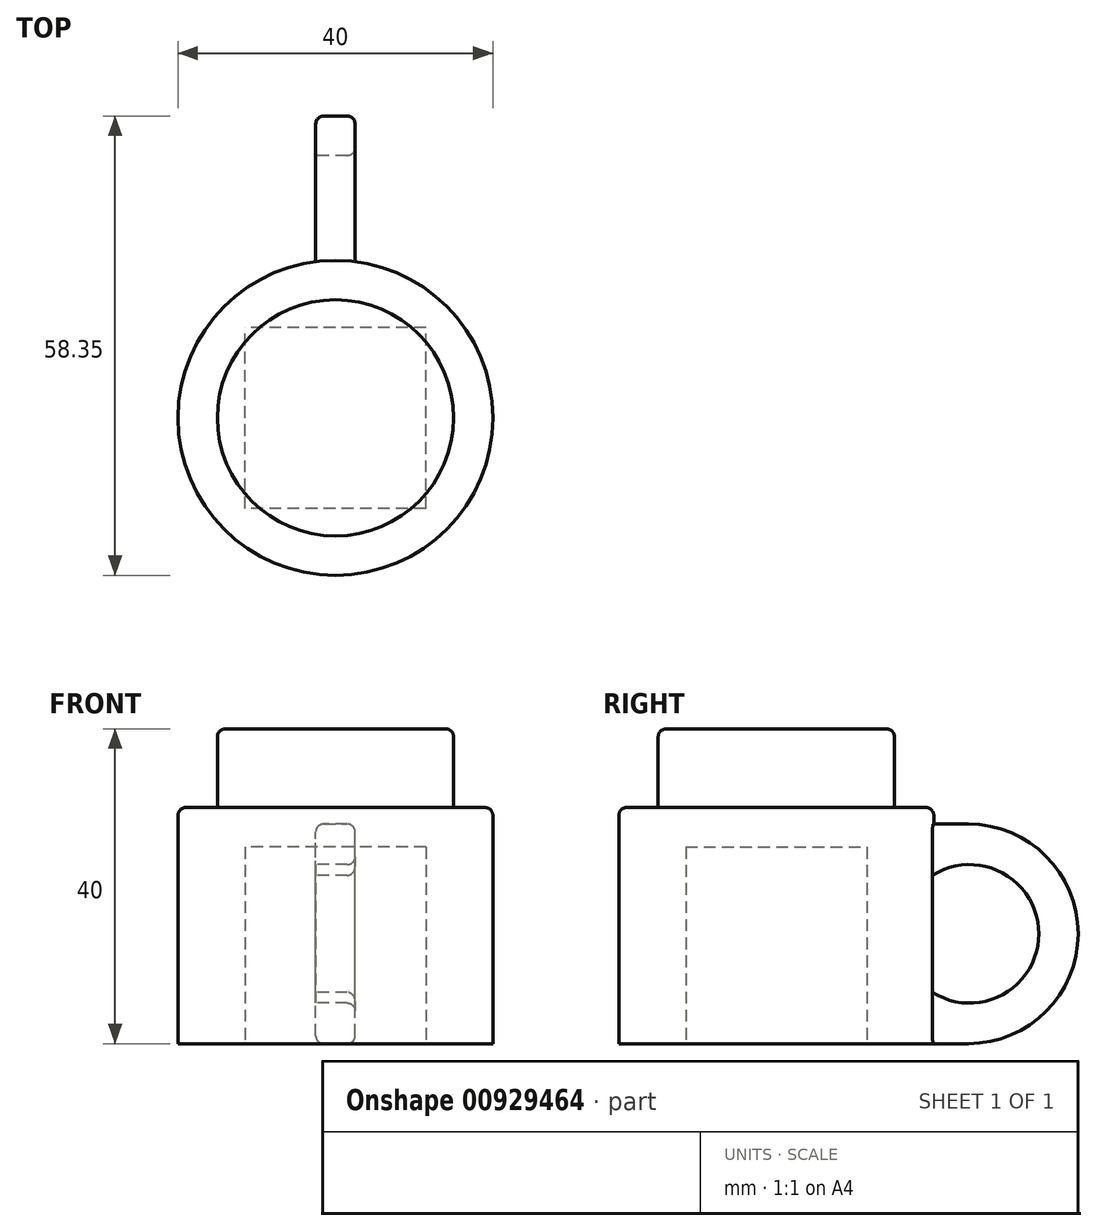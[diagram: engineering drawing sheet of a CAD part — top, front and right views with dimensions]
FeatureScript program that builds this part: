
annotation { "Feature Type Name" : "Feature", "Feature Type Description" : "" }
export const myFeature = defineFeature(function(context is Context, id is Id, definition is map)
    precondition{}
    {
        {
            var Q0;
            Q0=qCreatedBy(makeId("Top.planeOp"),FACE);
            var sketch = newSketch(context, id + "F0", { "sketchPlane" : qUnion([Q0])});
            skCircle(sketch, "E0", {"center": v(0, 0) * mm, "radius": 15 * mm});
            skSolve(sketch);
        }
        {
            var Q0;
            Q0=makeQuery(id+"F0.imprint","IMPRINT",FACE,{"disambiguationData":[TD([[makeQuery(id+"F0.imprint","IMPRINT",EDGE,{"derivedFrom":sQuery(id+"F0.wireOp",EDGE,"E0")}),1.0]])]});
            extrude(context, id + "F1", {"entities" : qUnion([Q0]), "depth" : 10 * mm, "offsetDistance" : 25 * mm});
        }
        {
            var Q0;
            Q0=qCreatedBy(makeId("Top.planeOp"),FACE);
            var sketch = newSketch(context, id + "F2", { "sketchPlane" : qUnion([Q0])});
            skCircle(sketch, "E1", {"center": v(0, 0) * mm, "radius": 20 * mm});
            skSolve(sketch);
        }
        {
            var Q0;
            Q0=makeQuery(id+"F2.imprint","IMPRINT",FACE,{"disambiguationData":[TD([[makeQuery(id+"F2.imprint","IMPRINT",EDGE,{"derivedFrom":sQuery(id+"F2.wireOp",EDGE,"E1")}),1.0]])]});
            extrude(context, id + "F3", {"entities" : qUnion([Q0]), "operationType" : NewBodyOperationType.ADD, "oppositeDirection" : true, "depth" : 30 * mm, "offsetDistance" : 25 * mm});
        }
        {
            var Q0;
            Q0=qCreatedBy(makeId("Right.planeOp"),FACE);
            var sketch = newSketch(context, id + "F4", { "sketchPlane" : qUnion([Q0])});
            skCircle(sketch, "E2", {"center": v(24.4, -16.05) * mm, "radius": 13.95 * mm});
            skPoint(sketch, "E2.first.point", {"position": v(11.59, -10.52) * mm});
            skPoint(sketch, "E2.second.point", {"position": v(37.23, -21.51) * mm});
            skPoint(sketch, "E2.third.point", {"position": v(35.11, -24.98) * mm});
            skLineSegment(sketch, "E3", {"start": v(-19.92, -30) * mm, "end": v(40.27, -30) * mm, "construction": true});
            skLineSegment(sketch, "E4", {"start": v(16.35, -30) * mm, "end": v(24.4, -30) * mm});
            skLineSegment(sketch, "E5", {"start": v(24.4, -30) * mm, "end": v(18.32, -26.87) * mm});
            skLineSegment(sketch, "E6", {"start": v(18.32, -26.87) * mm, "end": v(16.35, -30) * mm});
            skLineSegment(sketch, "E7", {"start": v(24.4, -2.1) * mm, "end": v(13.14, -2.1) * mm});
            skLineSegment(sketch, "E8", {"start": v(13.14, -2.1) * mm, "end": v(17.01, -7.58) * mm});
            skLineSegment(sketch, "E9", {"start": v(17.01, -7.58) * mm, "end": v(24.4, -2.1) * mm});
            skSolve(sketch);
        }
        {
            var Q0;
            Q0 = qSketchRegion(id + "F4", true);
            extrude(context, id + "F5", {"entities" : qUnion([Q0]), "operationType" : NewBodyOperationType.ADD, "depth" : 2.5 * mm, "offsetDistance" : 25 * mm, "hasSecondDirection" : true, "secondDirectionOppositeDirection" : true, "secondDirectionDepth" : 2.5 * mm});
        }
        {
            var Q0;
            {var subQ0=sQuery(id+"F4.wireOp",EDGE,"E2");Q0=makeQuery(id+"F5.boolean.opBoolean","SPLIT",FACE,{"disambiguationData":[TD([makeQuery(id+"F3.opExtrude","SWEPT_FACE",FACE,{"disambiguationData":[OSD([sQuery(id+"F2.wireOp",EDGE,"E1")])]})])],"derivedFrom":makeQuery(id+"F5.opExtrude","CAP_FACE",FACE,{"disambiguationData":[OSD([subQ0])],"isStart":true})});}
            var sketch = newSketch(context, id + "F6", { "sketchPlane" : qUnion([Q0])});
            skCircle(sketch, "E10", {"center": v(-24.55, -16.05) * mm, "radius": 8.8 * mm});
            skPoint(sketch, "E10.first.point", {"position": v(-33.35, -16.05) * mm});
            skPoint(sketch, "E10.first.point.positionSnap0", {"position": v(-19.84, -16.05) * mm});
            skPoint(sketch, "E10.second.point", {"position": v(-15.75, -16.05) * mm});
            skPoint(sketch, "E10.second.point.positionSnap0", {"position": v(-19.84, -16.05) * mm});
            skPoint(sketch, "E10.third.point", {"position": v(-19.84, -8.62) * mm});
            skSolve(sketch);
        }
        {
            var Q0;
            {var subQ0=sQuery(id+"F6.wireOp",EDGE,"E10");var subQ1=makeQuery(id+"F5.boolean.opBoolean","INTERSECT",EDGE,{"derivedFrom":[makeQuery(id+"F3.opExtrude","SWEPT_FACE",FACE,{"disambiguationData":[OSD([sQuery(id+"F2.wireOp",EDGE,"E1")])]}),makeQuery(id+"F5.opExtrude","CAP_FACE",FACE,{"disambiguationData":[OSD([sQuery(id+"F4.wireOp",EDGE,"E2")])],"isStart":true})]});var subQ2=makeQuery(id+"F6.imprint","INTERSECT",VERTEX,{"disambiguationData":[OD(0.0)],"derivedFrom":[subQ1,subQ0]});Q0=makeQuery(id+"F6.imprint","IMPRINT",FACE,{"disambiguationData":[TD([[makeQuery(id+"F6.imprint","IMPRINT",EDGE,{"disambiguationData":[TD([[subQ2,1.0]])],"derivedFrom":subQ0}),1.0]])]});}
            extrude(context, id + "F7", {"entities" : qUnion([Q0]), "operationType" : NewBodyOperationType.REMOVE, "oppositeDirection" : true, "depth" : 25 * mm, "offsetDistance" : 25 * mm});
        }
        {
            var Q0;
            Q0=makeQuery(id+"F3.opExtrude","CAP_FACE",FACE,{"disambiguationData":[OSD([sQuery(id+"F2.wireOp",EDGE,"E1")])],"isStart":false});
            var sketch = newSketch(context, id + "F8", { "sketchPlane" : qUnion([Q0])});
            skLineSegment(sketch, "E11.bottom", {"start": v(11.5, 11.5) * mm, "end": v(-11.5, 11.5) * mm});
            skLineSegment(sketch, "E11.top", {"start": v(11.5, -11.5) * mm, "end": v(-11.5, -11.5) * mm});
            skLineSegment(sketch, "E11.left", {"start": v(11.5, 11.5) * mm, "end": v(11.5, -11.5) * mm});
            skLineSegment(sketch, "E11.right", {"start": v(-11.5, 11.5) * mm, "end": v(-11.5, -11.5) * mm});
            skPoint(sketch, "E11.middle", {"position": v(0, 0) * mm});
            skSolve(sketch);
        }
        {
            var Q0;
            Q0=makeQuery(id+"F8.imprint","IMPRINT",FACE,{"disambiguationData":[TD([[makeQuery(id+"F8.imprint","IMPRINT",EDGE,{"derivedFrom":sQuery(id+"F8.wireOp",EDGE,"E11.bottom")}),1.0]])]});
            extrude(context, id + "F9", {"entities" : qUnion([Q0]), "operationType" : NewBodyOperationType.REMOVE, "oppositeDirection" : true, "depth" : 25 * mm, "offsetDistance" : 25 * mm});
        }
        {
            var Q0;
            Q0=makeQuery(id+"F1.opExtrude","CAP_EDGE",EDGE,{"disambiguationData":[OSD([sQuery(id+"F0.wireOp",EDGE,"E0")])],"isStart":false});
            var Q1;
            Q1=makeQuery(id+"F3.opExtrude","CAP_EDGE",EDGE,{"disambiguationData":[OSD([sQuery(id+"F2.wireOp",EDGE,"E1")])],"isStart":true});
            var Q2;
            Q2=makeQuery(id+"F5.opExtrude","CAP_EDGE",EDGE,{"disambiguationData":[OSD([sQuery(id+"F4.wireOp",EDGE,"E7")])],"isStart":false});
            var Q3;
            {var subQ0=sQuery(id+"F4.wireOp",EDGE,"E2");Q3=makeQuery(id+"F5.opExtrude","CAP_EDGE",EDGE,{"disambiguationData":[OSD([subQ0]),TDD([makeQuery(id+"F4.imprint","IMPRINT",EDGE,{"disambiguationData":[TD([[makeQuery(id+"F4.imprint","INTERSECT",VERTEX,{"derivedFrom":[subQ0,sQuery(id+"F4.wireOp",EDGE,"E4"),sQuery(id+"F4.wireOp",EDGE,"E5")]}),-1.0]])],"derivedFrom":subQ0})])],"isStart":true});}
            var Q4;
            Q4=makeQuery(id+"F7.boolean.opBoolean","INTERSECT",EDGE,{"derivedFrom":[makeQuery(id+"F5.opExtrude","CAP_FACE",FACE,{"disambiguationData":[OSD([sQuery(id+"F4.wireOp",EDGE,"E2"),sQuery(id+"F4.wireOp",EDGE,"E4"),sQuery(id+"F4.wireOp",EDGE,"E6"),sQuery(id+"F4.wireOp",EDGE,"E7"),sQuery(id+"F4.wireOp",EDGE,"E8")])],"isStart":false}),makeQuery(id+"F7.opExtrude","SWEPT_FACE",FACE,{"disambiguationData":[OSD([sQuery(id+"F6.wireOp",EDGE,"E10")])]})]});
            var Q5;
            Q5=makeQuery(id+"F1.opExtrude","CAP_EDGE",EDGE,{"disambiguationData":[OSD([sQuery(id+"F0.wireOp",EDGE,"E0")])],"isStart":true});
            fillet(context, id + "F10", {"entities" : qUnion([Q0, Q1, Q2, Q3, Q4, Q5]), "radius" : 1 * mm, "tangentPropagation" : true, "allowEdgeOverflow" : false});
        }
    });
